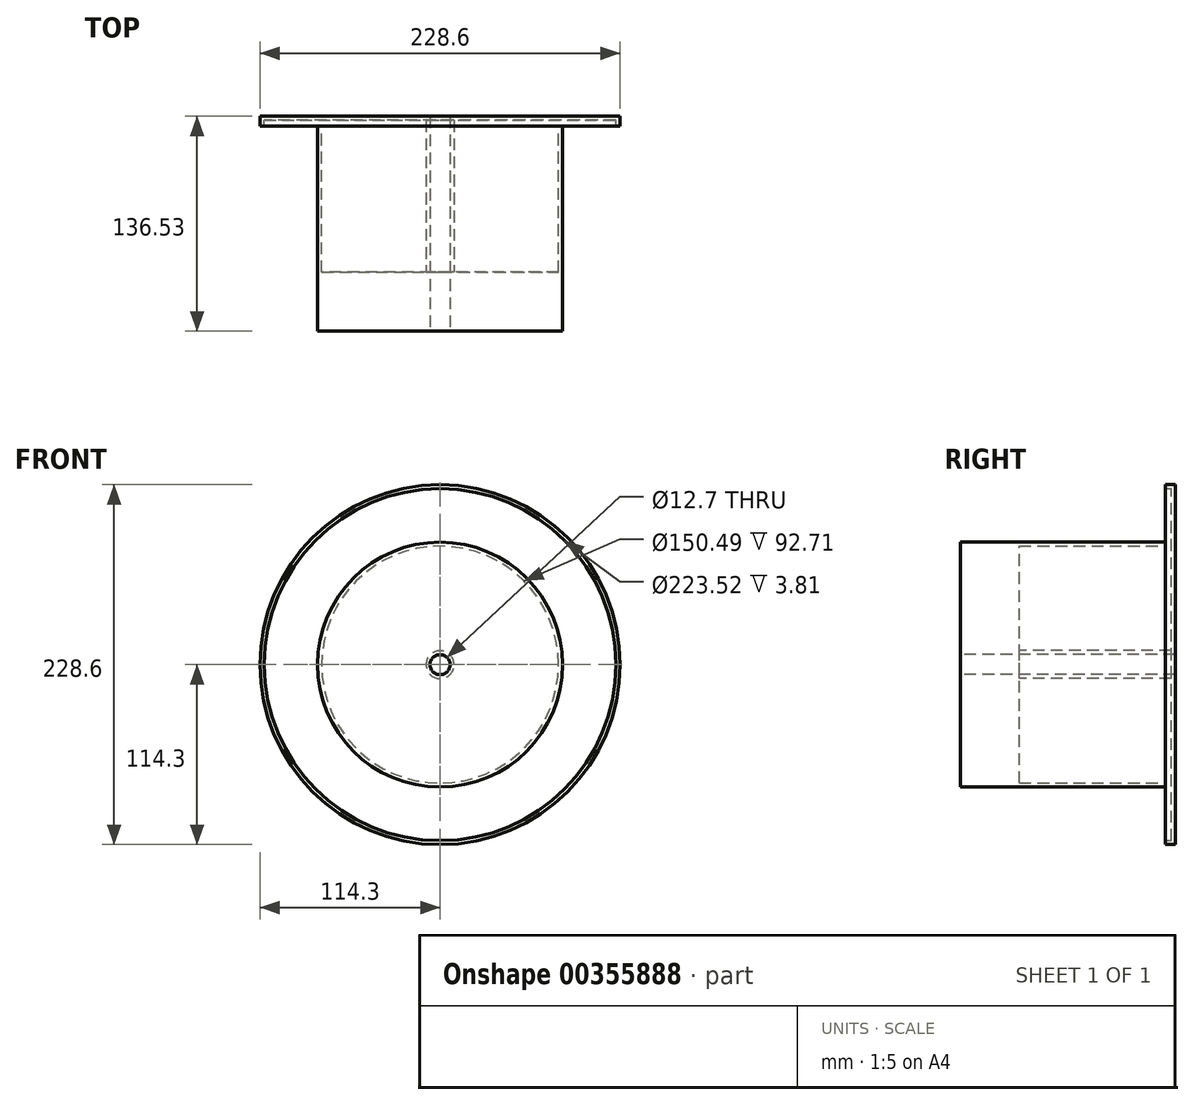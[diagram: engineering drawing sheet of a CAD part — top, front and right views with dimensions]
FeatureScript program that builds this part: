
annotation { "Feature Type Name" : "Feature", "Feature Type Description" : "" }
export const myFeature = defineFeature(function(context is Context, id is Id, definition is map)
    precondition{}
    {
        {
            var Q0;
            Q0=qCreatedBy(makeId("Front.planeOp"),FACE);
            var sketch = newSketch(context, id + "F0", { "sketchPlane" : qUnion([Q0])});
            skCircle(sketch, "E0", {"center": v(0, 0) * mm, "radius": 77.79 * mm});
            skCircle(sketch, "E1", {"center": v(0, 0) * mm, "radius": 114.3 * mm});
            skSolve(sketch);
        }
        {
            var Q0;
            Q0=makeQuery(id+"F0.imprint","IMPRINT",FACE,{"disambiguationData":[TD([[makeQuery(id+"F0.imprint","IMPRINT",EDGE,{"derivedFrom":sQuery(id+"F0.wireOp",EDGE,"E0")}),-1.0]])]});
            extrude(context, id + "F1", {"entities" : qUnion([Q0]), "depth" : 6.35 * mm});
        }
        {
            var Q0;
            Q0=makeQuery(id+"F0.imprint","IMPRINT",FACE,{"disambiguationData":[TD([[makeQuery(id+"F0.imprint","IMPRINT",EDGE,{"derivedFrom":sQuery(id+"F0.wireOp",EDGE,"E0")}),1.0]])]});
            extrude(context, id + "F2", {"entities" : qUnion([Q0]), "operationType" : NewBodyOperationType.ADD, "depth" : 203.2 * mm});
        }
        {
            var Q0;
            Q0=makeQuery(id+"F2.opExtrude","CAP_FACE",FACE,{"disambiguationData":[OSD([sQuery(id+"F0.wireOp",EDGE,"E0")])],"isStart":false});
            extrude(context, id + "F3", {"entities" : qUnion([Q0]), "operationType" : NewBodyOperationType.REMOVE, "oppositeDirection" : true, "depth" : 101.6 * mm});
        }
        {
            var Q0;
            Q0=makeQuery(id+"F3.boolean.opBoolean","COPY",FACE,{"derivedFrom":makeQuery(id+"F3.opExtrude","CAP_FACE",FACE,{"disambiguationData":[OSD([sQuery(id+"F0.wireOp",EDGE,"E0")])],"isStart":false})});
            var sketch = newSketch(context, id + "F4", { "sketchPlane" : qUnion([Q0])});
            skCircle(sketch, "E2", {"center": v(0, 0) * mm, "radius": 6.35 * mm});
            skSolve(sketch);
        }
        {
            var Q0;
            Q0=makeQuery(id+"F4.imprint","IMPRINT",FACE,{"disambiguationData":[TD([[makeQuery(id+"F4.imprint","IMPRINT",EDGE,{"derivedFrom":sQuery(id+"F4.wireOp",EDGE,"E2")}),1.0]])]});
            extrude(context, id + "F5", {"entities" : qUnion([Q0]), "operationType" : NewBodyOperationType.REMOVE, "endBound" : BoundingType.THROUGH_ALL, "oppositeDirection" : true, "depth" : 25.4 * mm});
        }
        {
            var Q0;
            Q0=makeQuery(id+"F1.opExtrude","CAP_FACE",FACE,{"disambiguationData":[OSD([sQuery(id+"F0.wireOp",EDGE,"E0"),sQuery(id+"F0.wireOp",EDGE,"E1")])],"isStart":false});
            shell(context, id + "F6", {"entities" : qUnion([Q0]), "thickness" : 2.54 * mm});
        }
        {
            var Q0;
            Q0=makeQuery(id+"F3.boolean.opBoolean","COPY",FACE,{"derivedFrom":makeQuery(id+"F3.opExtrude","CAP_FACE",FACE,{"disambiguationData":[OSD([sQuery(id+"F0.wireOp",EDGE,"E0")])],"isStart":false})});
            extrude(context, id + "F7", {"entities" : qUnion([Q0]), "operationType" : NewBodyOperationType.ADD, "depth" : 9.52 * mm});
        }
        {
            var Q0;
            Q0=makeQuery(id+"F7.opExtrude","CAP_FACE",FACE,{"disambiguationData":[OSD([sQuery(id+"F0.wireOp",EDGE,"E0")])],"isStart":false});
            extrude(context, id + "F8", {"entities" : qUnion([Q0]), "operationType" : NewBodyOperationType.ADD, "depth" : 25.4 * mm});
        }
    });
